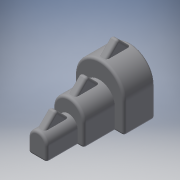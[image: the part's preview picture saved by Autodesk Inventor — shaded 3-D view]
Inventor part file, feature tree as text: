
AUTODESK INVENTOR PART (.ipt)
format: ipt  version: 2018 (Build 220112000, 112)  size: 372,224 bytes
history: native  units: in
note: dims shown in document units (in); Inventor stores cm internally (conversion verified against a paired STEP export)
features: extrude x12, sketch x12, fillet x6, reference x4, plane x1, projected_geometry x1
ambient origin geometry x8: Origin, YZ Plane, XZ Plane, XY Plane, X Axis, Y Axis, Z Axis, Center Point
bodies: Solid1 (feature_tree)
feature tree (36):
  extrude  "Extrusion1"  Depth=0.197in
  extrude  "Extrusion2"  Depth=0.4in
  extrude  "Extrusion3"  Depth=0.4in TaperAngle=0.0deg
  extrude  "Extrusion4"  Depth=1.0in TaperAngle=0.0deg
  extrude  "Extrusion5"  Depth=1.6in
  plane  "Work Plane1"
  extrude  "Extrusion8"  Depth=1.0in
  extrude  "Extrusion9"  Depth=0.25in
  extrude  "Extrusion10"  Depth=0.1065in
  extrude  "Extrusion11"  Depth=0.394in
  extrude  "Extrusion13"  Depth=0.25in TaperAngle=0.0deg
  extrude  "Extrusion14"  Depth=0.787in
  extrude  "Extrusion15"  Depth=0.394in
  fillet  "Fillet1"  Radius=0.25in
  fillet  "Fillet2"  Radius=0.1065in
  fillet  "Fillet3"  Radius=0.787in
  fillet  "Fillet4"  Radius=0.394in
  fillet  "Fillet5"  Radius=0.394in
  fillet  "Fillet6"  Radius=0.25in
  sketch  "Sketch1"  dims[d1=1.0in d2=0.0in d3=0.197in]
  reference  "Reference1"
  sketch  "Sketch2"  dims[d4=0.4in d5=0.0in d6=0.15in]
  reference  "Reference2"
  sketch  "Sketch3"  dims[d7=0.1772in d8=0.4in d9=0.0in]
  sketch  "Sketch4"  dims[d11=1.0in d12=0.0in d15=1.0in d16=0.0in]
  sketch  "Sketch5"  dims[d25=0.75in d26=1.6in]
  sketch  "Sketch8"  dims[d27=0.25in d28=1.0in]
  sketch  "Sketch9"  dims[d29=0.25in d30=0.6in]
  sketch  "Sketch10"  dims[d31=-0.8in d32=0.1065in]
  sketch  "Sketch11"  dims[d33=0.787in d34=0.394in]
  projected_geometry  "Projected Loop1"
  sketch  "Sketch14"  dims[d35=0.394in d36=0.25in d37=0.0in]
  reference  "Reference5"
  reference  "Reference6"
  sketch  "Sketch15"  dims[d38=0.1065in d39=0.787in]
  sketch  "Sketch16"  dims[d40=0.394in d41=0.394in d42=0.25in d43=0.0in d44=0.1065in d45=0.787in d46=0.394in d47=0.394in d48=0.25in d49=0.0in d50=0.0079in d51=0.0in d58=0.0394in d59=0.0394in d60=0.098in d61=0.098in d62=0.5in d63=0.0in d64=0.6605in d65=0.0in d66=0.25in d67=0.25in d68=0.6605in d69=0.0in d70=0.0787in d71=0.0787in d72=0.0787in d73=0.0787in d74=0.0394in d75=0.0394in]
